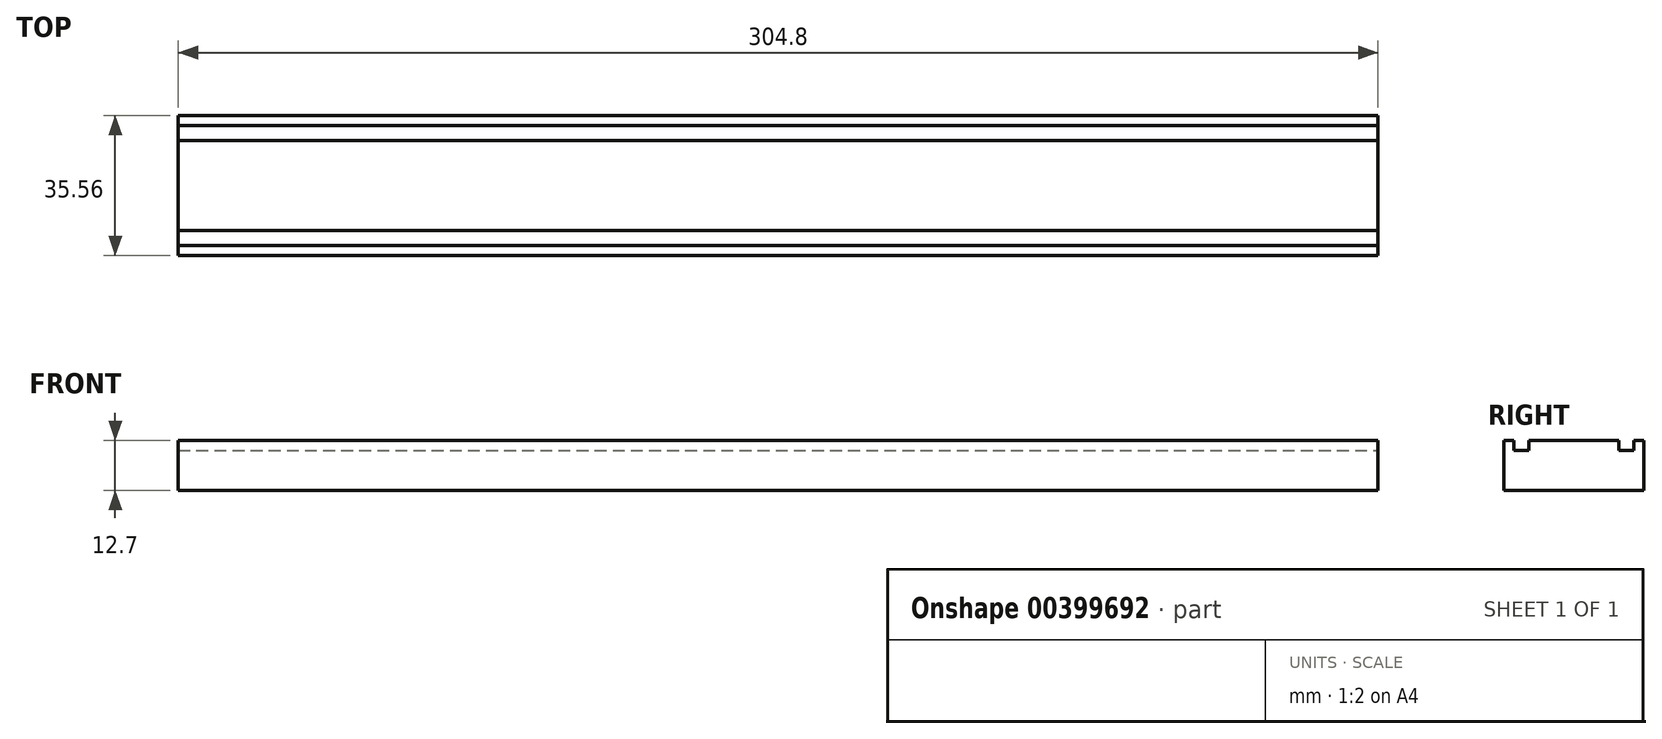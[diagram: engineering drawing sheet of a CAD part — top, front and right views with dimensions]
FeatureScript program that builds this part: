
annotation { "Feature Type Name" : "Feature", "Feature Type Description" : "" }
export const myFeature = defineFeature(function(context is Context, id is Id, definition is map)
    precondition{}
    {
        {
            var Q0;
            Q0=qCreatedBy(makeId("Top.planeOp"),FACE);
            var sketch = newSketch(context, id + "F0", { "sketchPlane" : qUnion([Q0])});
            skLineSegment(sketch, "E0.bottom", {"start": v(-152.4, 17.78) * mm, "end": v(152.4, 17.78) * mm});
            skLineSegment(sketch, "E0.top", {"start": v(-152.4, -17.78) * mm, "end": v(152.4, -17.78) * mm});
            skLineSegment(sketch, "E0.left", {"start": v(-152.4, 17.78) * mm, "end": v(-152.4, -17.78) * mm});
            skLineSegment(sketch, "E0.right", {"start": v(152.4, 17.78) * mm, "end": v(152.4, -17.78) * mm});
            skSolve(sketch);
        }
        {
            var Q0;
            Q0=makeQuery(id+"F0.imprint","IMPRINT",FACE,{"disambiguationData":[TD([[makeQuery(id+"F0.imprint","IMPRINT",EDGE,{"derivedFrom":sQuery(id+"F0.wireOp",EDGE,"E0.bottom")}),-1.0]])]});
            extrude(context, id + "F1", {"entities" : qUnion([Q0]), "depth" : 12.7 * mm});
        }
        {
            var Q0;
            Q0=makeQuery(id+"F1.opExtrude","CAP_FACE",FACE,{"disambiguationData":[OSD([sQuery(id+"F0.wireOp",EDGE,"E0.bottom"),sQuery(id+"F0.wireOp",EDGE,"E0.top"),sQuery(id+"F0.wireOp",EDGE,"E0.left"),sQuery(id+"F0.wireOp",EDGE,"E0.right")])],"isStart":false});
            var sketch = newSketch(context, id + "F2", { "sketchPlane" : qUnion([Q0])});
            skLineSegment(sketch, "E1", {"start": v(-152.4, 11.43) * mm, "end": v(152.4, 11.43) * mm});
            skLineSegment(sketch, "E2", {"start": v(152.4, 15.24) * mm, "end": v(-152.4, 15.24) * mm});
            skLineSegment(sketch, "E3", {"start": v(-152.4, 0) * mm, "end": v(152.4, 0) * mm, "construction": true});
            skLineSegment(sketch, "E4.MirrorCS", {"start": v(-152.4, -11.43) * mm, "end": v(152.4, -11.43) * mm});
            skLineSegment(sketch, "E5.MirrorCS", {"start": v(152.4, -15.24) * mm, "end": v(-152.4, -15.24) * mm});
            skSolve(sketch);
        }
        {
            var Q0;
            {var subQ0=sQuery(id+"F2.wireOp",EDGE,"E1");Q0=makeQuery(id+"F2.imprint","IMPRINT",FACE,{"disambiguationData":[TD([[makeQuery(id+"F2.imprint","IMPRINT",EDGE,{"derivedFrom":subQ0}),1.0]])]});}
            var Q1;
            {var subQ0=sQuery(id+"F2.wireOp",EDGE,"E4.MirrorCS");Q1=makeQuery(id+"F2.imprint","IMPRINT",FACE,{"disambiguationData":[TD([[makeQuery(id+"F2.imprint","IMPRINT",EDGE,{"derivedFrom":subQ0}),-1.0]])]});}
            extrude(context, id + "F3", {"entities" : qUnion([Q0, Q1]), "operationType" : NewBodyOperationType.REMOVE, "oppositeDirection" : true, "depth" : 2.54 * mm});
        }
    });
